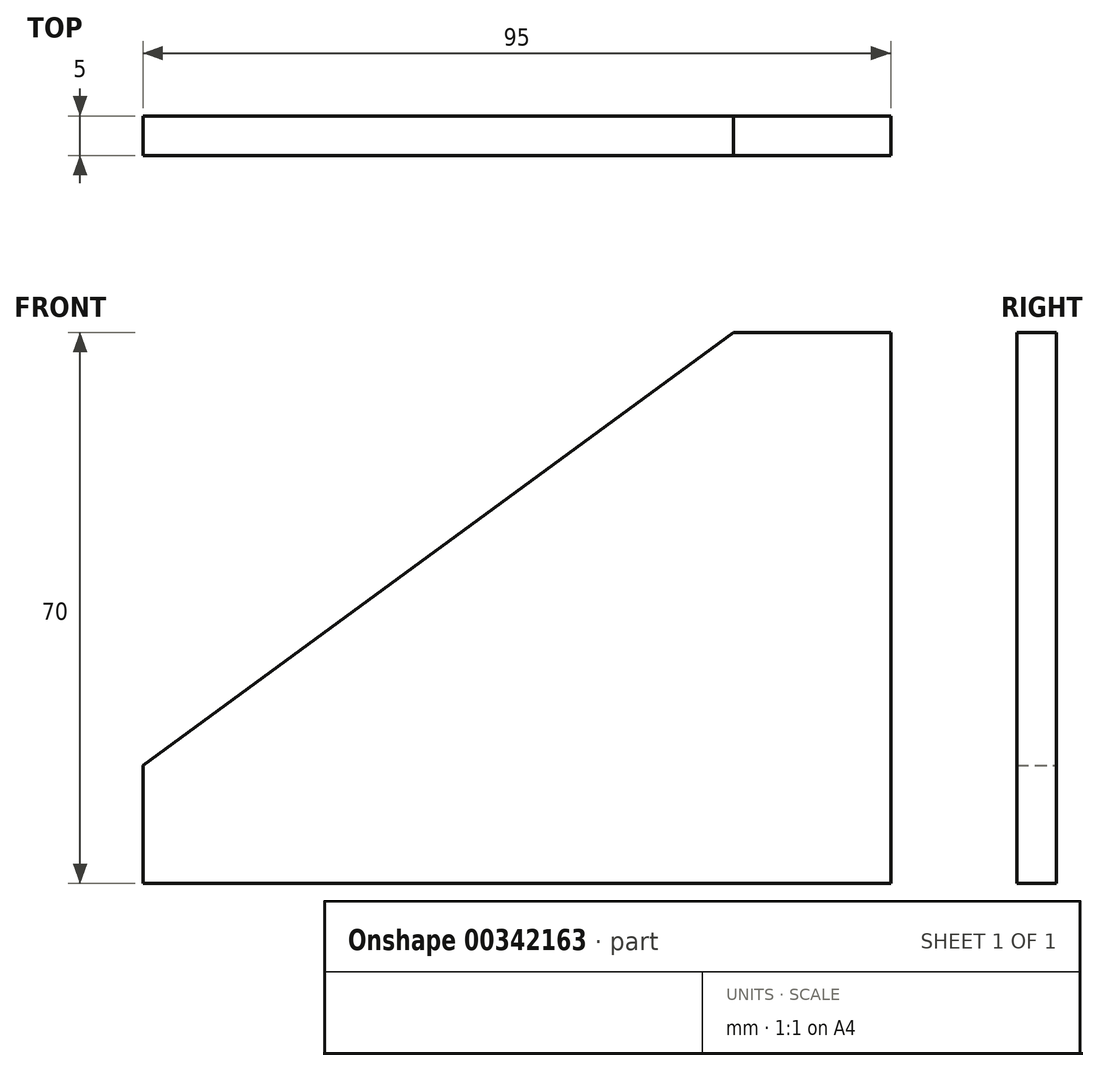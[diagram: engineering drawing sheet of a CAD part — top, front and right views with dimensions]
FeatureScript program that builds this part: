
annotation { "Feature Type Name" : "Feature", "Feature Type Description" : "" }
export const myFeature = defineFeature(function(context is Context, id is Id, definition is map)
    precondition{}
    {
        {
            var Q0;
            Q0=qCreatedBy(makeId("Front.planeOp"),FACE);
            var sketch = newSketch(context, id + "F0", { "sketchPlane" : qUnion([Q0])});
            skLineSegment(sketch, "E0.bottom", {"start": v(47.5, 35) * mm, "end": v(-47.5, 35) * mm});
            skLineSegment(sketch, "E0.top", {"start": v(47.5, -35) * mm, "end": v(-47.5, -35) * mm});
            skLineSegment(sketch, "E0.left", {"start": v(47.5, 35) * mm, "end": v(47.5, -35) * mm});
            skLineSegment(sketch, "E0.right", {"start": v(-47.5, 35) * mm, "end": v(-47.5, -35) * mm});
            skPoint(sketch, "E0.middle", {"position": v(0, 0) * mm});
            skLineSegment(sketch, "E1", {"start": v(-47.5, -20) * mm, "end": v(27.5, 35) * mm});
            skSolve(sketch);
        }
        {
            var Q0;
            {var subQ1=sQuery(id+"F0.wireOp",EDGE,"E0.top");Q0=makeQuery(id+"F0.imprint","IMPRINT",FACE,{"disambiguationData":[TD([[makeQuery(id+"F0.imprint","IMPRINT",EDGE,{"derivedFrom":subQ1}),-1.0]])]});}
            extrude(context, id + "F1", {"entities" : qUnion([Q0]), "depth" : 5 * mm});
        }
    });
